# Revit family: Loading-Dock-Equipment_Leveler_McGuire_Mechanical-EOD
name_source: partatom
category: Generic Models
units: mm (PartAtom-declared; Revit-internal decimal feet)

## family parameters
Can host rebar = No
Classification Number = 23.50.70.14.14
Cut with Voids When Loaded = No
Host = Face
Maintain Annotation Orientation = No
Part Type = Normal
Room Calculation Point = No
Round Connector Dimension = Use Diameter
Shared = No

## types (1)
- as Specified
    Assembly Code = E1030300
    Capacity = as Specified
    Deck Length = 2' - 3"
    Deck Width = 5' - 6"
    Default Elevation = 0' - 0"
    Description = McGuire Loading Dock Product as Specified
    Expected Lifespan (Years) = 0
    Fixture Material = Metal - McGuire - Finish as Specified
    Green Building-LEED = http://www.arcat.com
    Keynote = 11160
    Maintenance Schedule (Months) = 0
    Manufacturer = McGuire
    Manufacturer Fax = 262-255-4199
    Manufacturer Website = http://www.wbmcguire.com
    Model = As Specified
    Product Data = http://www.arcat.com
    Revision = R1_2017-01
    Sales Information = http://www.wbmcguire.com
    URL = http://www.wbmcguire.com
    Unit Depth = 1' - 3"
    Unit Height = 1' - 5"
    Unit Width = 8' - 8"
    Warranty Duration (Years) = 0

## geometry (parser evidence)
native form markers: Sweep x2
no freeform markers — native parametric forms only
